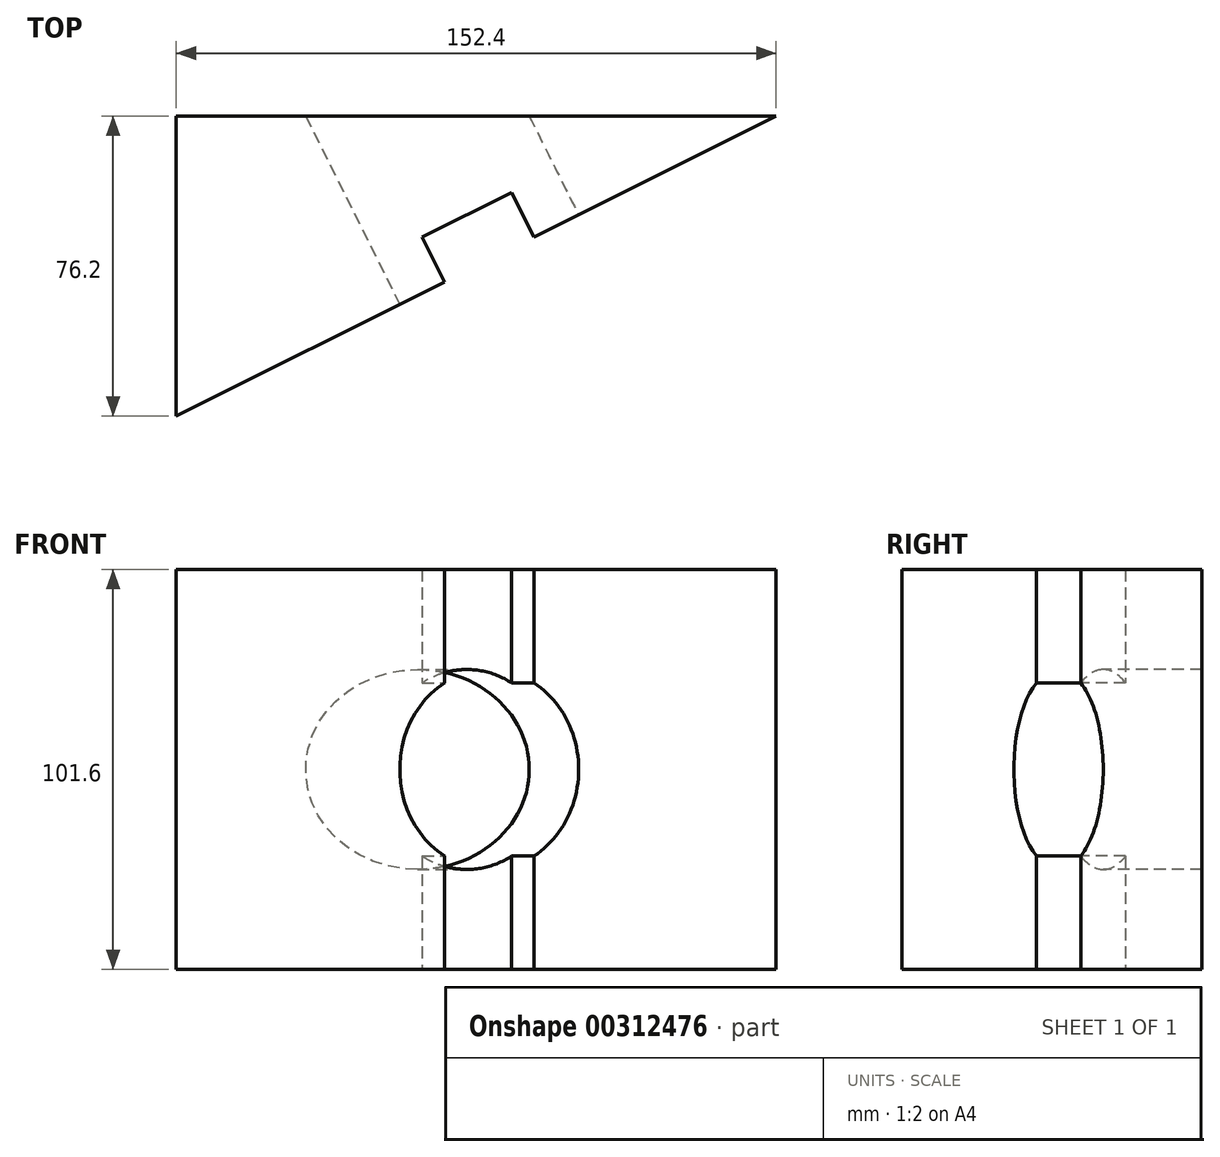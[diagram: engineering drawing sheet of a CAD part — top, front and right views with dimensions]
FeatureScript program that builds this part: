
annotation { "Feature Type Name" : "Feature", "Feature Type Description" : "" }
export const myFeature = defineFeature(function(context is Context, id is Id, definition is map)
    precondition{}
    {
        {
            var Q0;
            Q0=qCreatedBy(makeId("Top.planeOp"),FACE);
            var sketch = newSketch(context, id + "F0", { "sketchPlane" : qUnion([Q0])});
            skLineSegment(sketch, "E0.bottom", {"start": v(0, 0) * mm, "end": v(152.4, 0) * mm});
            skLineSegment(sketch, "E0.top", {"start": v(0, 76.2) * mm, "end": v(152.4, 76.2) * mm});
            skLineSegment(sketch, "E0.left", {"start": v(0, 0) * mm, "end": v(0, 76.2) * mm});
            skLineSegment(sketch, "E0.right", {"start": v(152.4, 0) * mm, "end": v(152.4, 76.2) * mm});
            skLineSegment(sketch, "E1", {"start": v(0, 0) * mm, "end": v(152.4, 76.2) * mm});
            skSolve(sketch);
        }
        {
            var Q0;
            Q0=makeQuery(id+"F0.imprint","IMPRINT",FACE,{"disambiguationData":[TD([[makeQuery(id+"F0.imprint","IMPRINT",EDGE,{"derivedFrom":sQuery(id+"F0.wireOp",EDGE,"E0.top")}),-1.0]])]});
            extrude(context, id + "F1", {"entities" : qUnion([Q0]), "depth" : 101.6 * mm});
        }
        {
            var Q0;
            Q0=makeQuery(id+"F1.opExtrude","SWEPT_FACE",FACE,{"disambiguationData":[OSD([sQuery(id+"F0.wireOp",EDGE,"E1")])]});
            var sketch = newSketch(context, id + "F2", { "sketchPlane" : qUnion([Q0])});
            skLineSegment(sketch, "E2.bottom", {"start": v(101.6, 101.6) * mm, "end": v(76.2, 101.6) * mm});
            skLineSegment(sketch, "E2.top", {"start": v(101.6, 0) * mm, "end": v(76.2, 0) * mm});
            skLineSegment(sketch, "E2.left", {"start": v(101.6, 101.6) * mm, "end": v(101.6, 0) * mm});
            skLineSegment(sketch, "E2.right", {"start": v(76.2, 101.6) * mm, "end": v(76.2, 0) * mm});
            skPoint(sketch, "E2.middle", {"position": v(88.9, 50.8) * mm});
            skSolve(sketch);
        }
        {
            var Q0;
            Q0=makeQuery(id+"F2.imprint","IMPRINT",FACE,{"disambiguationData":[TD([[makeQuery(id+"F2.imprint","IMPRINT",EDGE,{"derivedFrom":sQuery(id+"F2.wireOp",EDGE,"E2.bottom")}),-1.0]])]});
            extrude(context, id + "F3", {"entities" : qUnion([Q0]), "operationType" : NewBodyOperationType.REMOVE, "oppositeDirection" : true, "depth" : 12.7 * mm});
        }
        {
            var Q0;
            {var subQ0=sQuery(id+"F0.wireOp",EDGE,"E1");var subQ1=sQuery(id+"F0.wireOp",EDGE,"E0.left");Q0=makeQuery(id+"F3.boolean.opBoolean","SPLIT",FACE,{"disambiguationData":[TD([makeQuery(id+"F1.opExtrude","SWEPT_FACE",FACE,{"disambiguationData":[OSD([subQ1])]})])],"derivedFrom":makeQuery(id+"F1.opExtrude","SWEPT_FACE",FACE,{"disambiguationData":[OSD([subQ0])]})});}
            var sketch = newSketch(context, id + "F4", { "sketchPlane" : qUnion([Q0])});
            skCircle(sketch, "E3", {"center": v(88.9, 50.8) * mm, "radius": 25.4 * mm});
            skSolve(sketch);
        }
        {
            var Q0;
            Q0=qSketchRegion(id+"F4",true);
            extrude(context, id + "F5", {"entities" : qUnion([Q0]), "operationType" : NewBodyOperationType.REMOVE, "endBound" : BoundingType.THROUGH_ALL, "oppositeDirection" : true, "depth" : 24.13 * mm});
        }
    });
